# Revit family: FP-Revit18-E402BLXFD4-Fridges
name_source: partatom
category: Specialty Equipment
revit_build: Autodesk Revit 2018 (Build: 20170223_1515(x64)
units: mm (PartAtom-declared; Revit-internal decimal feet)

## family parameters
Always vertical = Yes
Cut with Voids When Loaded = Yes
OmniClass Number = 23.40.40.11.11.17
OmniClass Title = Refrigerator-Freezer
Part Type = Normal
Room Calculation Point = No
Round Connector Dimension = Use Diameter
Shared = No
Work Plane-Based = No

## types (1)
- E402BLXFD4
    Cavity - Depth = 625 mm  [stored 2.05052 ft]
    Cavity - Height = 1735 mm  [stored 5.69226 ft]
    Cavity - Width = 675 mm  [stored 2.21457 ft]
    Chassis - Depth = 625 mm  [stored 2.05052 ft]
    Chassis - Height = 1664 mm
    Chassis - Width = 635 mm
    Connector Description - Electrical = 230 V, 50Hz
    Description = 63.5cm Freestanding Refrigerator with Bottom Freezer
    Manufacturer = Fisher & Paykel Appliances
    Material - Body = Fisher & Paykel - Grey
    Material - Door Front = Fisher & Paykel - Stainless Steel
    Material - Door Structure = Fisher & Paykel - White
    Material - Handle = Fisher & Paykel - Aluminium
    Material - Logo = Fisher & Paykel - Steel, Chrome Plated
    Model = E402BLXFD4
    Product - Depth = 736 mm  [stored 2.4147 ft]
    Product - Height = 1720 mm
    Product - Width = 635 mm
    URL = www.fisherpaykel.com
    Visibility - Clearance Required = Yes

note: [stored X ft] marks values corroborated as IEEE doubles in the binary element streams (Revit-internal decimal feet)

## geometry (parser evidence)
native form markers: Sweep x2
no freeform markers — native parametric forms only
